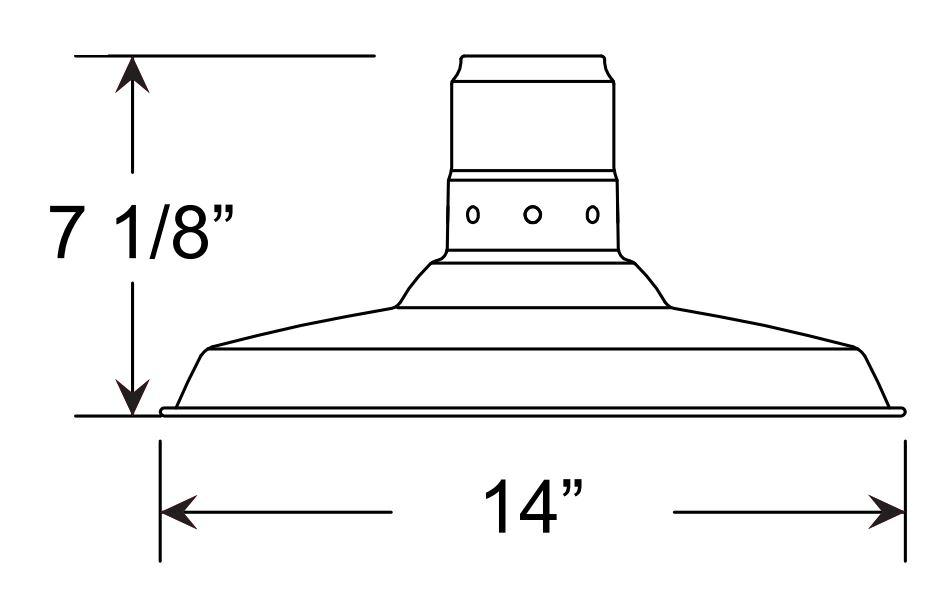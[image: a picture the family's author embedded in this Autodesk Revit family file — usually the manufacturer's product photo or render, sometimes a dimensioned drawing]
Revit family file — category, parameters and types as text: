
# Revit family: MILKCAN(8,10,12,18)MB
name_source: partatom
category: Lighting Fixtures
units: mm (PartAtom-declared; Revit-internal decimal feet)

## family parameters
Always vertical = Yes
Cut with Voids When Loaded = No
Light Source = Yes
OmniClass Number = 23.80.70.00
OmniClass Title = Lighting
Part Type = Normal
Room Calculation Point = No
Round Connector Dimension = Use Diameter
Shared = No
Work Plane-Based = No

## types (4) — shared parameters
Body Colour = Spun aluminium
Body Material = body
CRI = >90
Color Filter = 16777215
Construction Material = Heavy Duty spun aluminum.
Default Elevation = 0' - 0"
Description = 120-277 Voltage
Dimming = 1%
Dimming Lamp Color Temperature Shift = <None>
Efficiency = 65-125 lumens per watt
Lamp = MB
Life = L70 50,000 hours
Load Classification = Lighting
Manufacturer = ANP Lighting
Photometric Web File = MC18M024LDN40K.ies
Power Factor = 1
Tilt Angle = 90.00°
URL = https://www.anplighting.com
Voltage = 277 V
Warranty = 5 year limited warranty

## per-type parameters (varying)
| type | Apparent Load | Fixture Diameter | Fixture Height | MC10 | MC12 | MC18 | MC8 | Wattage Comments | Weight |
| MC08 | 100 VA | 0' - 8" | 0' - 4" | No | No | No | Yes | 100W Max | 1 lbs |
| MC10 | 100 VA | 0' - 10" | 0' - 4" | Yes | No | No | No | 100W Max | 1 lbs |
| MC12 | 200 VA | 1' - 0" | 0' - 5" | No | Yes | No | No | 200W  Max | 1.5 lbs |
| MC18 | 200 VA | 1' - 6" | 0' - 6" | No | No | Yes | No | 200W Max | 2 lbs |

note: column(s) folded — value = type name in every type: Model

## geometry (parser evidence)
native form markers: Sweep x40
no freeform markers — native parametric forms only
